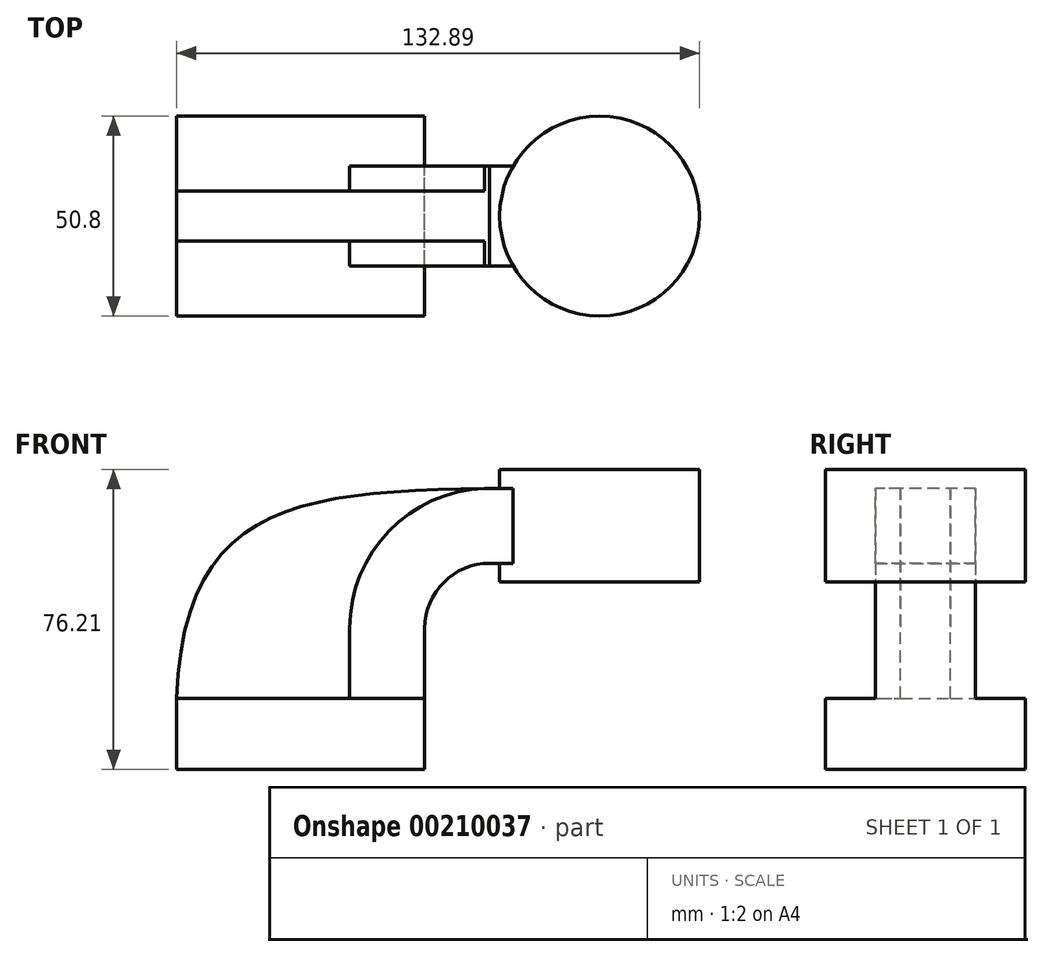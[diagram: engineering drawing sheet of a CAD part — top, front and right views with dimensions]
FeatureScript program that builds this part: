
annotation { "Feature Type Name" : "Feature", "Feature Type Description" : "" }
export const myFeature = defineFeature(function(context is Context, id is Id, definition is map)
    precondition{}
    {
        {
            var Q0;
            Q0=qCreatedBy(makeId("Front.planeOp"),FACE);
            var sketch = newSketch(context, id + "F0", { "sketchPlane" : qUnion([Q0])});
            skLineSegment(sketch, "E0.bottom", {"start": v(31.52, 9.02) * mm, "end": v(-31.52, 9.02) * mm});
            skLineSegment(sketch, "E0.top", {"start": v(31.52, -9.02) * mm, "end": v(-31.52, -9.02) * mm});
            skLineSegment(sketch, "E0.left", {"start": v(31.52, 9.02) * mm, "end": v(31.52, -9.02) * mm});
            skLineSegment(sketch, "E0.right", {"start": v(-31.52, 9.02) * mm, "end": v(-31.52, -9.02) * mm});
            skPoint(sketch, "E0.middle", {"position": v(0, 0) * mm});
            skLineSegment(sketch, "E1", {"start": v(31.52, 9.02) * mm, "end": v(31.52, 26.87) * mm});
            skArc(sketch, "E2", {"start": v(31.52, 26.87) * mm, "mid": v(36.36, 38.55) * mm, "end": v(48.03, 43.38) * mm});
            skLineSegment(sketch, "E3.bottom", {"start": v(101.37, 38.62) * mm, "end": v(50.57, 38.62) * mm});
            skLineSegment(sketch, "E3.top", {"start": v(101.37, 67.2) * mm, "end": v(50.57, 67.2) * mm});
            skLineSegment(sketch, "E3.left", {"start": v(101.37, 38.62) * mm, "end": v(101.37, 67.2) * mm});
            skLineSegment(sketch, "E3.right", {"start": v(50.57, 38.62) * mm, "end": v(50.57, 67.2) * mm});
            skPoint(sketch, "E3.middle", {"position": v(75.97, 52.9) * mm});
            skLineSegment(sketch, "E4", {"start": v(48.03, 43.38) * mm, "end": v(75.97, 43.38) * mm});
            skLineSegment(sketch, "E5.0", {"start": v(48.03, 62.43) * mm, "end": v(75.97, 62.43) * mm});
            skArc(sketch, "E5.1", {"start": v(12.47, 26.87) * mm, "mid": v(22.89, 52.02) * mm, "end": v(48.03, 62.43) * mm});
            skLineSegment(sketch, "E5.2", {"start": v(12.47, 9.02) * mm, "end": v(12.47, 26.87) * mm});
            skLineSegment(sketch, "E6", {"start": v(75.97, 62.43) * mm, "end": v(75.97, 43.38) * mm});
            skFitSpline(sketch, "E7", {"points": [v(-31.52, 9.02) * mm, v(48.03, 62.43) * mm], "startDerivative": vector(5.3, 149.94) * mm, "endDerivative": vector(144.1, 2.52) * mm});
            skLineSegment(sketch, "E8", {"start": v(75.97, 67.2) * mm, "end": v(75.97, 38.62) * mm});
            skSolve(sketch);
        }
        {
            var Q0;
            Q0=makeQuery(id+"F0.imprint","IMPRINT",FACE,{"disambiguationData":[TD([[makeQuery(id+"F0.imprint","IMPRINT",EDGE,{"derivedFrom":sQuery(id+"F0.wireOp",EDGE,"E0.top")}),-1.0]])]});
            extrude(context, id + "F1", {"entities" : qUnion([Q0]), "endBound" : BoundingType.SYMMETRIC, "depth" : 50.8 * mm});
        }
        {
            var Q0;
            {var subQ10=sQuery(id+"F0.wireOp",EDGE,"E1");Q0=makeQuery(id+"F0.imprint","IMPRINT",FACE,{"disambiguationData":[TD([[makeQuery(id+"F0.imprint","IMPRINT",EDGE,{"derivedFrom":subQ10}),1.0]])]});}
            var Q1;
            {var subQ0=sQuery(id+"F0.wireOp",EDGE,"E4");var subQ1=sQuery(id+"F0.wireOp",EDGE,"E3.right");var subQ2=makeQuery(id+"F0.imprint","INTERSECT",VERTEX,{"derivedFrom":[subQ1,subQ0]});Q1=makeQuery(id+"F0.imprint","IMPRINT",FACE,{"disambiguationData":[TD([[makeQuery(id+"F0.imprint","IMPRINT",EDGE,{"disambiguationData":[TD([[subQ2,-1.0]])],"derivedFrom":subQ1}),-1.0]])]});}
            extrude(context, id + "F2", {"entities" : qUnion([Q0, Q1]), "operationType" : NewBodyOperationType.ADD, "endBound" : BoundingType.SYMMETRIC, "depth" : 25.4 * mm});
        }
        {
            var Q0;
            {var subQ4=sQuery(id+"F0.wireOp",EDGE,"E3.left");Q0=makeQuery(id+"F0.imprint","IMPRINT",FACE,{"disambiguationData":[TD([[makeQuery(id+"F0.imprint","IMPRINT",EDGE,{"derivedFrom":subQ4}),1.0]])]});}
            var Q1;
            Q1=sQuery(id+"F0.wireOp",EDGE,"E6");
            revolve(context, id + "F3", {"operationType" : NewBodyOperationType.ADD, "entities" : qUnion([Q0]), "axis" : qUnion([Q1]), "revolveType" : RevolveType.FULL});
        }
        {
            var Q0;
            {var subQ3=sQuery(id+"F0.wireOp",EDGE,"E5.2");Q0=makeQuery(id+"F0.imprint","IMPRINT",FACE,{"disambiguationData":[TD([[makeQuery(id+"F0.imprint","IMPRINT",EDGE,{"derivedFrom":subQ3}),1.0]])]});}
            extrude(context, id + "F4", {"entities" : qUnion([Q0]), "operationType" : NewBodyOperationType.ADD, "endBound" : BoundingType.SYMMETRIC, "depth" : 12.7 * mm});
        }
    });
